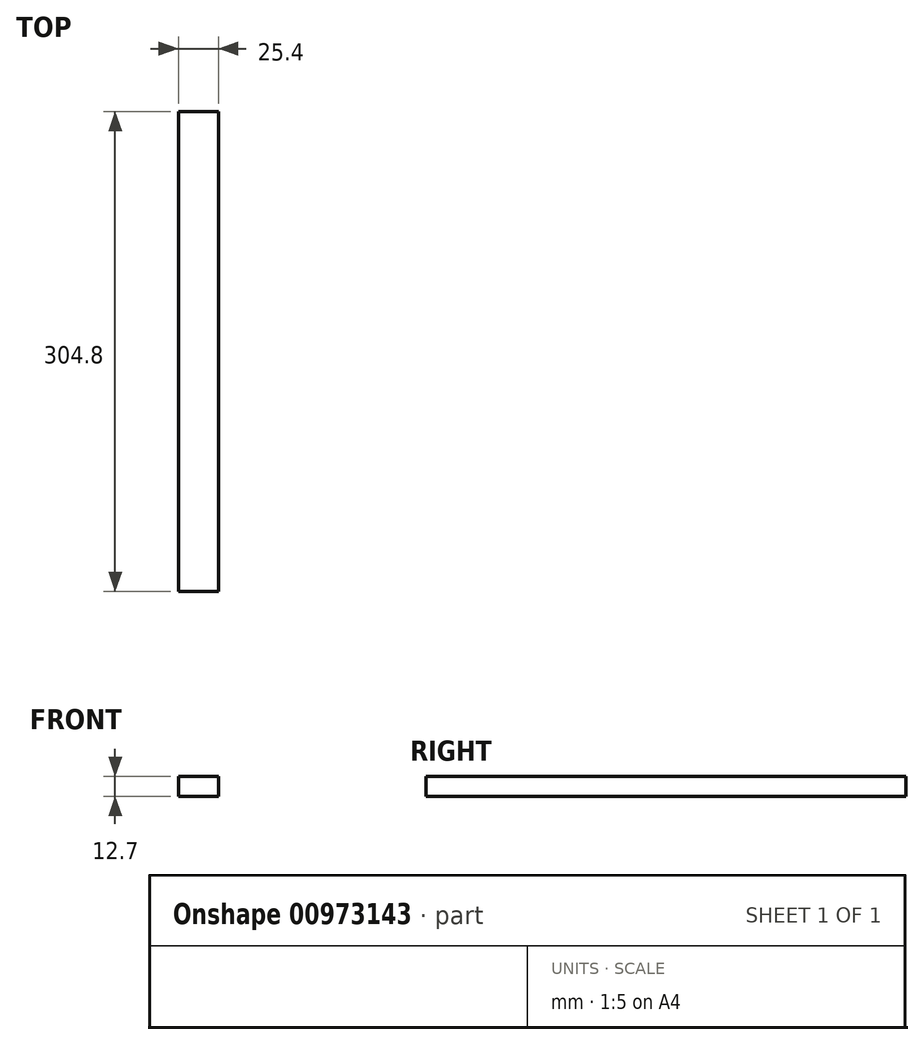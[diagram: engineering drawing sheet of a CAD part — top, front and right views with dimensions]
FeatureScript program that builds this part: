
annotation { "Feature Type Name" : "Feature", "Feature Type Description" : "" }
export const myFeature = defineFeature(function(context is Context, id is Id, definition is map)
    precondition{}
    {
        {
            var Q0;
            Q0=qCreatedBy(makeId("Top.planeOp"),FACE);
            var sketch = newSketch(context, id + "F0", { "sketchPlane" : qUnion([Q0])});
            skLineSegment(sketch, "E0", {"start": v(0, -74.68) * mm, "end": v(-12.7, -74.68) * mm});
            skLineSegment(sketch, "E1.MirrorCS", {"start": v(0, -74.68) * mm, "end": v(12.7, -74.68) * mm});
            skLineSegment(sketch, "E2", {"start": v(-12.7, 230.12) * mm, "end": v(12.7, 230.12) * mm});
            skLineSegment(sketch, "E3", {"start": v(-12.7, 230.12) * mm, "end": v(-12.7, -74.68) * mm});
            skLineSegment(sketch, "E4", {"start": v(12.7, 230.12) * mm, "end": v(12.7, -74.68) * mm});
            skSolve(sketch);
        }
        {
            var Q0;
            Q0=makeQuery(id+"F0.imprint","IMPRINT",FACE,{"disambiguationData":[TD([[makeQuery(id+"F0.imprint","IMPRINT",EDGE,{"derivedFrom":sQuery(id+"F0.wireOp",EDGE,"E0")}),-1.0]])]});
            extrude(context, id + "F1", {"entities" : qUnion([Q0]), "endBound" : BoundingType.SYMMETRIC, "depth" : 12.7 * mm, "offsetDistance" : 25.4 * mm});
        }
    });
